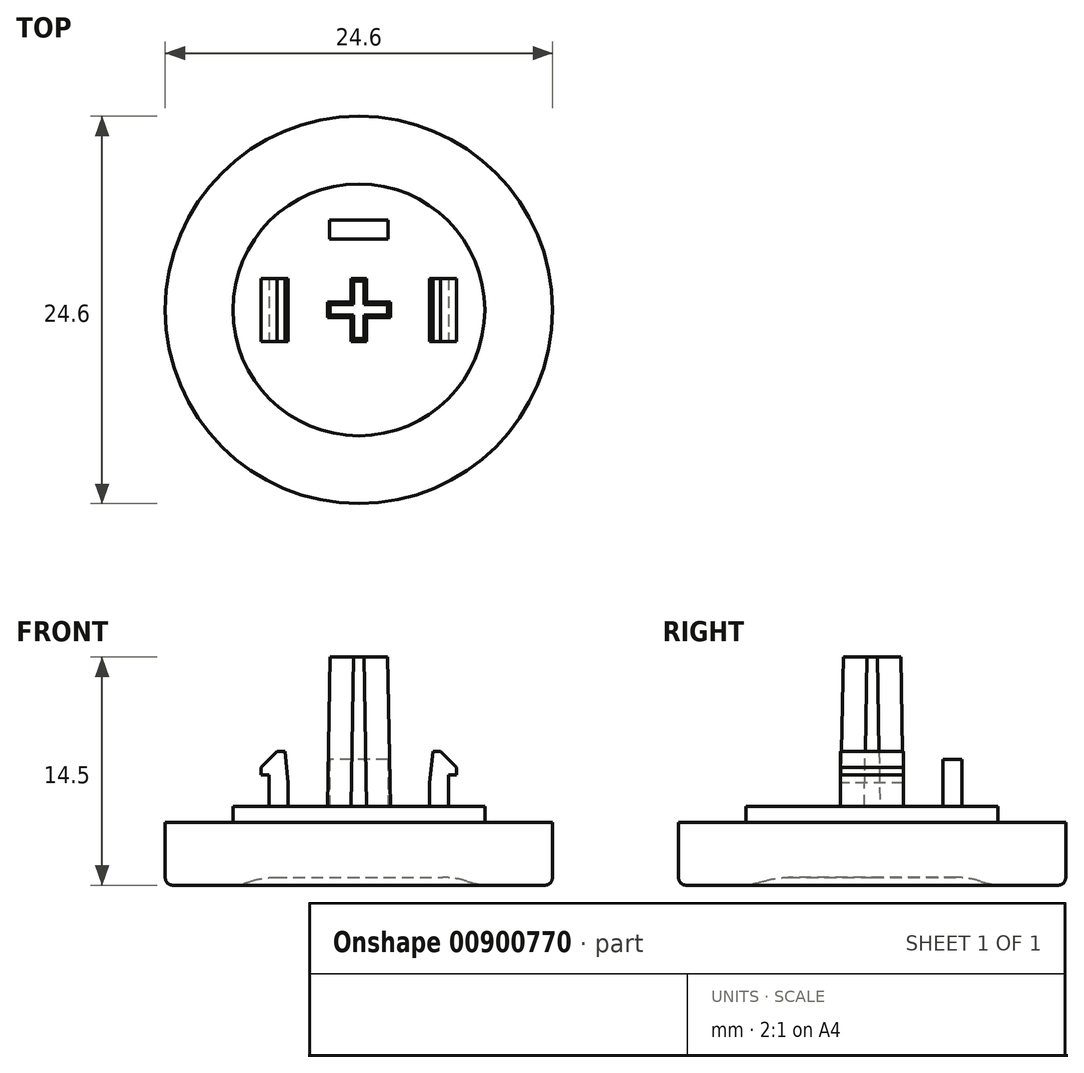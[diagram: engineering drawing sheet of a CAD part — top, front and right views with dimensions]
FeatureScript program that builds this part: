
annotation { "Feature Type Name" : "Feature", "Feature Type Description" : "" }
export const myFeature = defineFeature(function(context is Context, id is Id, definition is map)
    precondition{}
    {
        {
            var Q0;
            Q0=qCreatedBy(makeId("Top.planeOp"),FACE);
            var sketch = newSketch(context, id + "F0", { "sketchPlane" : qUnion([Q0])});
            skCircle(sketch, "E0", {"center": v(0, 0) * mm, "radius": 8 * mm});
            skSolve(sketch);
        }
        {
            var Q0;
            Q0=makeQuery(id+"F0.imprint","IMPRINT",FACE,{"disambiguationData":[TD([[makeQuery(id+"F0.imprint","IMPRINT",EDGE,{"derivedFrom":sQuery(id+"F0.wireOp",EDGE,"E0")}),1.0]])]});
            extrude(context, id + "F1", {"entities" : qUnion([Q0]), "depth" : 1 * mm, "offsetDistance" : 25 * mm});
        }
        {
            var Q0;
            Q0=makeQuery(id+"F1.opExtrude","CAP_FACE",FACE,{"disambiguationData":[OSD([sQuery(id+"F0.wireOp",EDGE,"E0")])],"isStart":false});
            var sketch = newSketch(context, id + "F2", { "sketchPlane" : qUnion([Q0])});
            skLineSegment(sketch, "E1.bottom", {"start": v(0.5, 2) * mm, "end": v(-0.5, 2) * mm});
            skLineSegment(sketch, "E1.top", {"start": v(0.5, -2) * mm, "end": v(-0.5, -2) * mm});
            skLineSegment(sketch, "E1.left", {"start": v(0.5, 2) * mm, "end": v(0.5, 0.5) * mm});
            skLineSegment(sketch, "E1.right", {"start": v(-0.5, 2) * mm, "end": v(-0.5, 0.5) * mm});
            skPoint(sketch, "E1.middle", {"position": v(0, 0) * mm});
            skLineSegment(sketch, "E2.bottom", {"start": v(2, -0.5) * mm, "end": v(0.5, -0.5) * mm});
            skLineSegment(sketch, "E2.top", {"start": v(2, 0.5) * mm, "end": v(0.5, 0.5) * mm});
            skLineSegment(sketch, "E2.left", {"start": v(2, -0.5) * mm, "end": v(2, 0.5) * mm});
            skLineSegment(sketch, "E2.right", {"start": v(-2, -0.5) * mm, "end": v(-2, 0.5) * mm});
            skLineSegment(sketch, "E3.trimOffspring", {"start": v(-0.5, 0.5) * mm, "end": v(-2, 0.5) * mm});
            skLineSegment(sketch, "E4.trimOffspring", {"start": v(0.5, -0.5) * mm, "end": v(0.5, -2) * mm});
            skLineSegment(sketch, "E5.trimOffspring", {"start": v(-0.5, -0.5) * mm, "end": v(-0.5, -2) * mm});
            skLineSegment(sketch, "E6.trimOffspring", {"start": v(-0.5, -0.5) * mm, "end": v(-2, -0.5) * mm});
            skSolve(sketch);
        }
        {
            var Q0;
            Q0 = qSketchRegion(id + "F2", true);
            extrude(context, id + "F3", {"entities" : qUnion([Q0]), "operationType" : NewBodyOperationType.ADD, "depth" : 9.5 * mm, "offsetDistance" : 25 * mm, "hasDraft" : true, "draftAngle" : 1 * degree, "draftPullDirection" : true});
        }
        {
            var Q0;
            Q0=qCreatedBy(makeId("Front.planeOp"),FACE);
            var sketch = newSketch(context, id + "F4", { "sketchPlane" : qUnion([Q0])});
            skLineSegment(sketch, "E7", {"start": v(4.5, 1) * mm, "end": v(4.5, 2.5) * mm});
            skLineSegment(sketch, "E8", {"start": v(4.5, 2.5) * mm, "end": v(4.7, 4.5) * mm});
            skLineSegment(sketch, "E9", {"start": v(6.2, 3.5) * mm, "end": v(6.2, 3) * mm});
            skLineSegment(sketch, "E10", {"start": v(6.2, 3) * mm, "end": v(5.7, 3) * mm});
            skLineSegment(sketch, "E11", {"start": v(5.7, 3) * mm, "end": v(5.7, 1) * mm});
            skLineSegment(sketch, "E12", {"start": v(5.7, 1) * mm, "end": v(4.5, 1) * mm});
            skPoint(sketch, "E13.start.orphan", {"position": v(5.7, 4.5) * mm});
            skLineSegment(sketch, "E14", {"start": v(6.2, 3.5) * mm, "end": v(5.2, 4.5) * mm});
            skLineSegment(sketch, "E15", {"start": v(5.2, 4.5) * mm, "end": v(4.7, 4.5) * mm});
            skLineSegment(sketch, "E16.MirrorCS", {"start": v(-6.2, 3.5) * mm, "end": v(-5.2, 4.5) * mm});
            skLineSegment(sketch, "E17.MirrorCS", {"start": v(-6.2, 3.5) * mm, "end": v(-6.2, 3) * mm});
            skLineSegment(sketch, "E18.MirrorCS", {"start": v(-6.2, 3) * mm, "end": v(-5.7, 3) * mm});
            skLineSegment(sketch, "E19.MirrorCS", {"start": v(-5.7, 3) * mm, "end": v(-5.7, 1) * mm});
            skLineSegment(sketch, "E20.MirrorCS", {"start": v(-5.7, 1) * mm, "end": v(-4.5, 1) * mm});
            skLineSegment(sketch, "E21.MirrorCS", {"start": v(-4.5, 1) * mm, "end": v(-4.5, 2.5) * mm});
            skLineSegment(sketch, "E22.MirrorCS", {"start": v(-4.5, 2.5) * mm, "end": v(-4.7, 4.5) * mm});
            skLineSegment(sketch, "E23.MirrorCS", {"start": v(-5.2, 4.5) * mm, "end": v(-4.7, 4.5) * mm});
            skSolve(sketch);
        }
        {
            var Q0;
            Q0=makeQuery(id+"F4.imprint","IMPRINT",FACE,{"disambiguationData":[TD([[makeQuery(id+"F4.imprint","IMPRINT",EDGE,{"derivedFrom":sQuery(id+"F4.wireOp",EDGE,"E7")}),-1.0]])]});
            var Q1;
            Q1=makeQuery(id+"F4.imprint","IMPRINT",FACE,{"disambiguationData":[TD([[makeQuery(id+"F4.imprint","IMPRINT",EDGE,{"derivedFrom":sQuery(id+"F4.wireOp",EDGE,"E16.MirrorCS")}),-1.0]])]});
            extrude(context, id + "F5", {"entities" : qUnion([Q0, Q1]), "operationType" : NewBodyOperationType.ADD, "endBound" : BoundingType.SYMMETRIC, "oppositeDirection" : true, "depth" : 4 * mm, "offsetDistance" : 25 * mm});
        }
        {
            var Q0;
            Q0=makeQuery(id+"F1.opExtrude","CAP_FACE",FACE,{"disambiguationData":[OSD([sQuery(id+"F0.wireOp",EDGE,"E0")])],"isStart":false});
            var sketch = newSketch(context, id + "F6", { "sketchPlane" : qUnion([Q0])});
            skLineSegment(sketch, "E24.bottom", {"start": v(1.85, 4.5) * mm, "end": v(-1.85, 4.5) * mm});
            skLineSegment(sketch, "E24.top", {"start": v(1.85, 5.7) * mm, "end": v(-1.85, 5.7) * mm});
            skLineSegment(sketch, "E24.left", {"start": v(1.85, 4.5) * mm, "end": v(1.85, 5.7) * mm});
            skLineSegment(sketch, "E24.right", {"start": v(-1.85, 4.5) * mm, "end": v(-1.85, 5.7) * mm});
            skPoint(sketch, "E24.middle", {"position": v(0, 5.1) * mm});
            skSolve(sketch);
        }
        {
            var Q0;
            Q0 = qSketchRegion(id + "F6", true);
            extrude(context, id + "F7", {"entities" : qUnion([Q0]), "operationType" : NewBodyOperationType.ADD, "depth" : 3 * mm, "offsetDistance" : 25 * mm});
        }
        {
            var Q0;
            Q0=makeQuery(id+"F1.opExtrude","CAP_FACE",FACE,{"disambiguationData":[OSD([sQuery(id+"F0.wireOp",EDGE,"E0")])],"isStart":true});
            var sketch = newSketch(context, id + "F8", { "sketchPlane" : qUnion([Q0])});
            skCircle(sketch, "E25", {"center": v(0, 0) * mm, "radius": 12.3 * mm});
            skSolve(sketch);
        }
        {
            var Q0;
            Q0 = qSketchRegion(id + "F8", true);
            extrude(context, id + "F9", {"entities" : qUnion([Q0]), "operationType" : NewBodyOperationType.ADD, "depth" : 4 * mm, "offsetDistance" : 25 * mm});
        }
        {
            var Q0;
            Q0=makeQuery(id+"F9.opExtrude","CAP_EDGE",EDGE,{"disambiguationData":[OSD([sQuery(id+"F8.wireOp",EDGE,"E25")])],"isStart":false});
            fillet(context, id + "F10", {"entities" : qUnion([Q0]), "radius" : 0.5 * mm, "tangentPropagation" : true, "allowEdgeOverflow" : false});
        }
        {
            var Q0;
            Q0=makeQuery(id+"F9.opExtrude","CAP_FACE",FACE,{"disambiguationData":[OSD([sQuery(id+"F8.wireOp",EDGE,"E25")])],"isStart":false});
            var sketch = newSketch(context, id + "F11", { "sketchPlane" : qUnion([Q0])});
            skCircle(sketch, "E26", {"center": v(0, 0) * mm, "radius": 7.5 * mm});
            skSolve(sketch);
        }
        {
            var Q0;
            Q0 = qSketchRegion(id + "F11", true);
            extrude(context, id + "F12", {"entities" : qUnion([Q0]), "operationType" : NewBodyOperationType.REMOVE, "oppositeDirection" : true, "depth" : 0.5 * mm, "offsetDistance" : 25 * mm});
        }
        {
            var Q0;
            Q0=makeQuery(id+"F12.boolean.opBoolean","COPY",EDGE,{"derivedFrom":makeQuery(id+"F12.opExtrude","CAP_EDGE",EDGE,{"disambiguationData":[OSD([sQuery(id+"F11.wireOp",EDGE,"E26")])],"isStart":false})});
            fillet(context, id + "F13", {"entities" : qUnion([Q0]), "radius" : 5 * mm, "tangentPropagation" : true, "allowEdgeOverflow" : false});
        }
        {
            var Q0;
            Q0=makeQuery(id+"F13.opFillet","BLEND_EDGE",EDGE,{"blendedFrom":[makeQuery(id+"F12.boolean.opBoolean","COPY",EDGE,{"derivedFrom":makeQuery(id+"F12.opExtrude","CAP_EDGE",EDGE,{"disambiguationData":[OSD([sQuery(id+"F11.wireOp",EDGE,"E26")])],"isStart":false})}),makeQuery(id+"F9.opExtrude","CAP_FACE",FACE,{"disambiguationData":[OSD([sQuery(id+"F8.wireOp",EDGE,"E25")])],"isStart":false})],"blendedInto":[makeQuery(id+"F9.opExtrude","CAP_FACE",FACE,{"disambiguationData":[OSD([sQuery(id+"F8.wireOp",EDGE,"E25")])],"isStart":false})]});
            fillet(context, id + "F14", {"entities" : qUnion([Q0]), "radius" : 5 * mm, "tangentPropagation" : true, "allowEdgeOverflow" : false});
        }
    });
